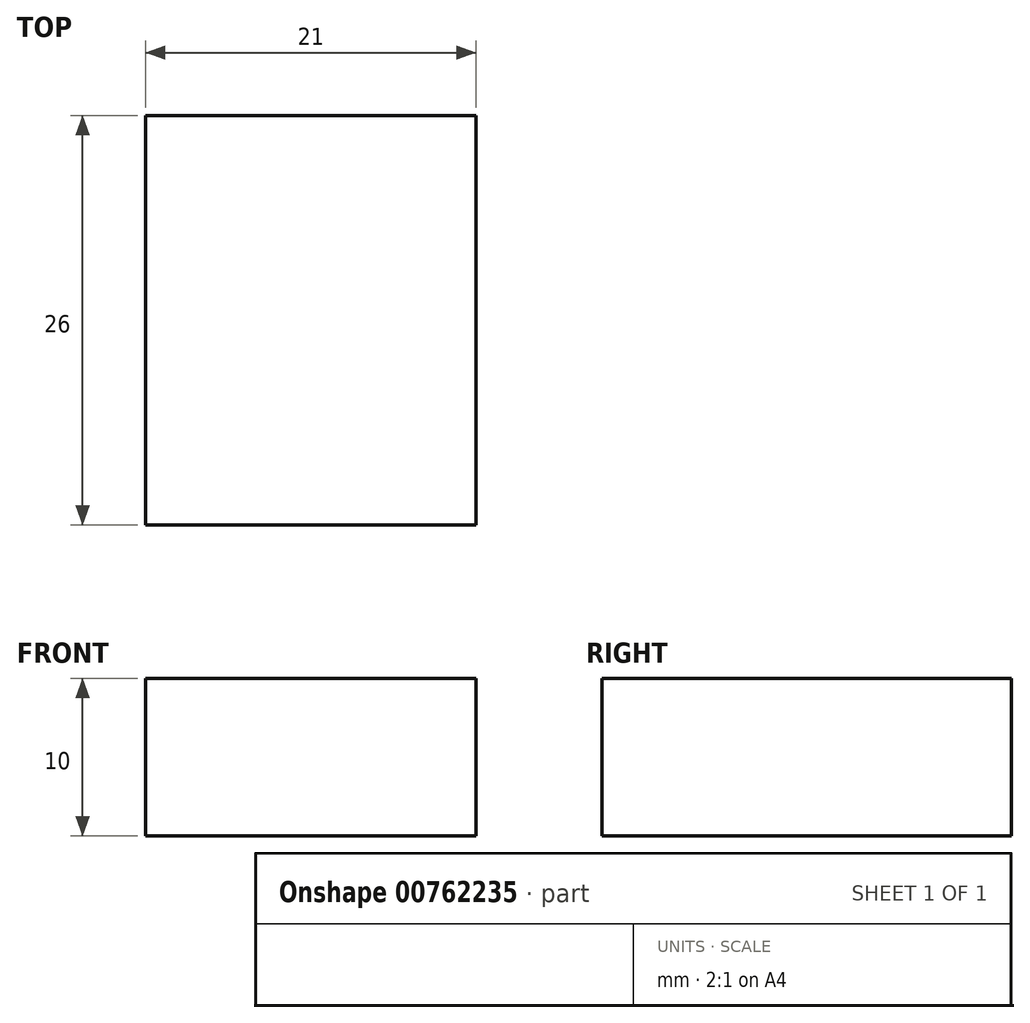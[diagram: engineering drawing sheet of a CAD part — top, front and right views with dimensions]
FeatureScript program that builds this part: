
annotation { "Feature Type Name" : "Feature", "Feature Type Description" : "" }
export const myFeature = defineFeature(function(context is Context, id is Id, definition is map)
    precondition{}
    {
        {
            var Q0;
            Q0=qCreatedBy(makeId("Top.planeOp"), FACE);
            var sketch = newSketch(context, id + "F0", { "sketchPlane" : qUnion([Q0])});
            skLineSegment(sketch, "E0.bottom", {"start": v(-10.5, 13) * mm, "end": v(10.5, 13) * mm});
            skLineSegment(sketch, "E0.top", {"start": v(-10.5, -13) * mm, "end": v(10.5, -13) * mm});
            skLineSegment(sketch, "E0.left", {"start": v(-10.5, 13) * mm, "end": v(-10.5, -13) * mm});
            skLineSegment(sketch, "E0.right", {"start": v(10.5, 13) * mm, "end": v(10.5, -13) * mm});
            skSolve(sketch);
        }
        {
            var Q0;
            Q0 = qSketchRegion(id + "F0", true);
            extrude(context, id + "F1", {"entities" : qUnion([Q0]), "depth" : 10 * mm, "offsetDistance" : 25 * mm});
        }
    });
